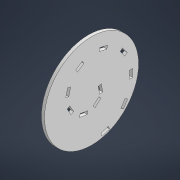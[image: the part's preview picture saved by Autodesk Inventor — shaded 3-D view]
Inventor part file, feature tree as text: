
AUTODESK INVENTOR PART (.ipt)
format: ipt  version: 2022 (Build 260153000, 153)  size: 269,312 bytes
history: native  units: mm
features: other x3, extrude x2, sketch x2, projected_geometry x1
ambient origin geometry x8: Origin, YZ Plane, XZ Plane, XY Plane, X Axis, Y Axis, Z Axis, Center Point
bodies: Body1 (feature_tree)
feature tree (8):
  other  "Твердое тело1"
  extrude  "Выдавливание1"  Depth=10.0mm TaperAngle=0.0deg
  sketch  "Эскиз2"
  extrude  "Выдавливание2"  Depth=4.0mm TaperAngle=0.0deg
  sketch  "Эскиз1"
  other  "Кривая по 2D-формуле1"
  other  "Кривая по 2D-формуле2"
  projected_geometry  "Спроецированная петля1"
